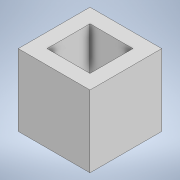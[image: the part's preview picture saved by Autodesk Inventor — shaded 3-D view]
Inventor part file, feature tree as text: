
AUTODESK INVENTOR PART (.ipt)
format: ipt  version: 2022 (Build 260153000, 153)  size: 99,840 bytes
history: native  units: in
note: dims shown in document units (in); Inventor stores cm internally (conversion verified against a paired STEP export)
features: extrude x1, shell x1, sketch x1
ambient origin geometry x8: Origin, YZ Plane, XZ Plane, XY Plane, X Axis, Y Axis, Z Axis, Center Point
bodies: Solid1 (feature_tree)
feature tree (3):
  extrude  "Extrusion1"  Depth=0.1969in
  shell  "Shell1"  Thickness=0.1969in
  sketch  "Sketch1"  dims[d0=0.1969in d1=0.1969in d2=0.1969in d3=0.0in d4=0.0394in]
